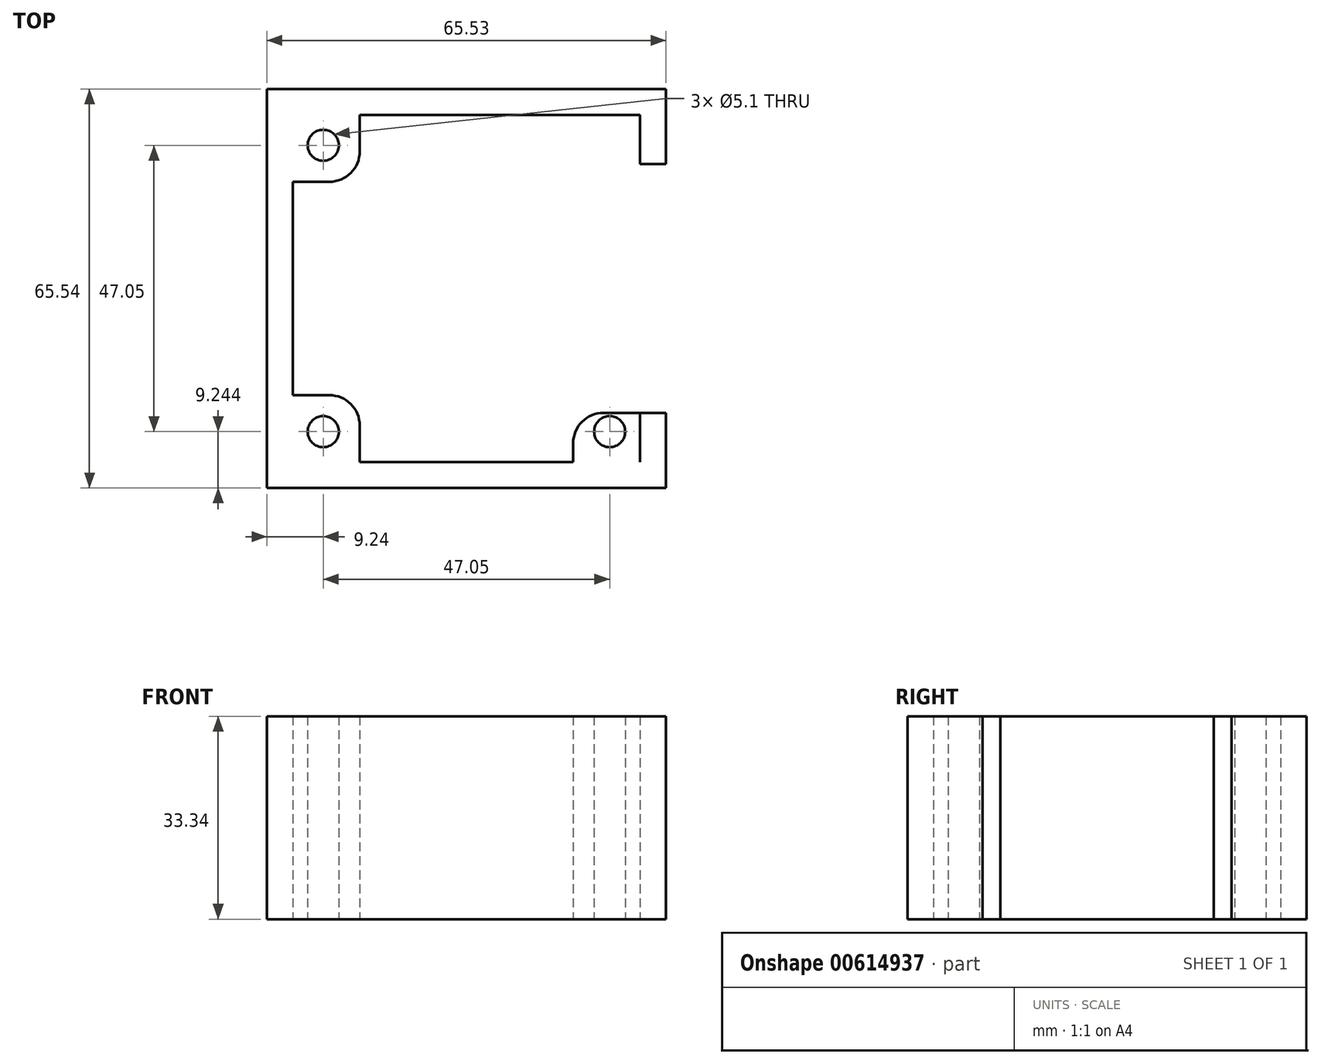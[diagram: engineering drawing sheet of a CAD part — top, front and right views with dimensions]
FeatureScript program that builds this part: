
annotation { "Feature Type Name" : "Feature", "Feature Type Description" : "" }
export const myFeature = defineFeature(function(context is Context, id is Id, definition is map)
    precondition{}
    {
        {
            var Q0;
            Q0=qCreatedBy(makeId("Top.planeOp"),FACE);
            var sketch = newSketch(context, id + "F0", { "sketchPlane" : qUnion([Q0])});
            skLineSegment(sketch, "E0", {"start": v(57.55, -8.14) * mm, "end": v(-2.45, -8.14) * mm});
            skLineSegment(sketch, "E1.bottom", {"start": v(26.08, 20.38) * mm, "end": v(-30.97, 20.38) * mm});
            skLineSegment(sketch, "E1.top", {"start": v(26.08, -36.67) * mm, "end": v(-30.97, -36.67) * mm});
            skLineSegment(sketch, "E1.left", {"start": v(26.08, 20.38) * mm, "end": v(26.08, -36.67) * mm});
            skLineSegment(sketch, "E1.right", {"start": v(-30.97, 20.38) * mm, "end": v(-30.97, -36.67) * mm});
            skPoint(sketch, "E1.middle", {"position": v(-2.45, -8.14) * mm});
            skLineSegment(sketch, "E2.bottom", {"start": v(30.32, 24.63) * mm, "end": v(-35.21, 24.63) * mm});
            skLineSegment(sketch, "E2.top", {"start": v(30.32, -40.9) * mm, "end": v(-35.21, -40.9) * mm});
            skLineSegment(sketch, "E2.left", {"start": v(30.32, 24.63) * mm, "end": v(30.32, -40.9) * mm});
            skLineSegment(sketch, "E2.right", {"start": v(-35.21, 24.63) * mm, "end": v(-35.21, -40.9) * mm});
            skLineSegment(sketch, "E3", {"start": v(26.08, 20.38) * mm, "end": v(30.32, 24.63) * mm});
            skLineSegment(sketch, "E4", {"start": v(26.08, 20.38) * mm, "end": v(26.08, 12.3) * mm});
            skLineSegment(sketch, "E5", {"start": v(26.08, 12.3) * mm, "end": v(30.32, 12.3) * mm});
            skLineSegment(sketch, "E6", {"start": v(30.32, 12.3) * mm, "end": v(30.32, 24.63) * mm});
            skLineSegment(sketch, "E7.MirrorCS", {"start": v(26.08, -28.57) * mm, "end": v(30.33, -28.57) * mm});
            skLineSegment(sketch, "E8.MirrorCS", {"start": v(30.33, -28.57) * mm, "end": v(30.33, -40.9) * mm});
            skLineSegment(sketch, "E9", {"start": v(26.08, -28.57) * mm, "end": v(26.08, -36.67) * mm});
            skLineSegment(sketch, "E10", {"start": v(-30.97, 20.38) * mm, "end": v(-25.97, 15.38) * mm});
            skCircle(sketch, "E11", {"center": v(-25.97, 15.38) * mm, "radius": 2.55 * mm});
            skLineSegment(sketch, "E12.bottom", {"start": v(-30.97, 20.38) * mm, "end": v(-19.97, 20.38) * mm});
            skLineSegment(sketch, "E12.top", {"start": v(-30.97, 9.38) * mm, "end": v(-24.97, 9.38) * mm});
            skLineSegment(sketch, "E12.left", {"start": v(-30.97, 20.38) * mm, "end": v(-30.97, 9.38) * mm});
            skLineSegment(sketch, "E12.right", {"start": v(-19.97, 20.38) * mm, "end": v(-19.97, 14.38) * mm});
            skPoint(sketch, "E13.visualSharp", {"position": v(-19.97, 9.38) * mm});
            skArc(sketch, "E13.filletArc", {"start": v(-24.97, 9.38) * mm, "mid": v(-21.43, 10.85) * mm, "end": v(-19.97, 14.38) * mm});
            skLineSegment(sketch, "E14", {"start": v(26.08, 20.38) * mm, "end": v(21.08, 15.38) * mm});
            skCircle(sketch, "E15", {"center": v(21.08, 15.38) * mm, "radius": 2.55 * mm});
            skLineSegment(sketch, "E16", {"start": v(26.08, 12.3) * mm, "end": v(20.08, 12.3) * mm});
            skLineSegment(sketch, "E17", {"start": v(15.08, 17.3) * mm, "end": v(15.08, 20.38) * mm});
            skPoint(sketch, "E18.visualSharp", {"position": v(15.08, 12.3) * mm});
            skArc(sketch, "E18.filletArc", {"start": v(15.08, 17.3) * mm, "mid": v(16.54, 13.76) * mm, "end": v(20.08, 12.3) * mm});
            skLineSegment(sketch, "E19", {"start": v(-30.97, -36.67) * mm, "end": v(-25.97, -31.67) * mm});
            skLineSegment(sketch, "E20", {"start": v(-19.97, -36.67) * mm, "end": v(-19.97, -30.67) * mm});
            skLineSegment(sketch, "E21", {"start": v(-24.97, -25.67) * mm, "end": v(-30.97, -25.67) * mm});
            skPoint(sketch, "E22.visualSharp", {"position": v(-19.97, -25.67) * mm});
            skArc(sketch, "E22.filletArc", {"start": v(-19.97, -30.67) * mm, "mid": v(-21.43, -27.13) * mm, "end": v(-24.97, -25.67) * mm});
            skCircle(sketch, "E23", {"center": v(-25.97, -31.67) * mm, "radius": 2.55 * mm});
            skLineSegment(sketch, "E24", {"start": v(26.08, -36.67) * mm, "end": v(21.08, -31.67) * mm});
            skLineSegment(sketch, "E25", {"start": v(15.08, -33.57) * mm, "end": v(15.08, -36.67) * mm});
            skCircle(sketch, "E26", {"center": v(21.08, -31.67) * mm, "radius": 2.55 * mm});
            skLineSegment(sketch, "E27", {"start": v(26.08, -28.57) * mm, "end": v(20.08, -28.57) * mm});
            skLineSegment(sketch, "E28", {"start": v(15.08, -33.57) * mm, "end": v(15.08, -33.57) * mm});
            skPoint(sketch, "E29.visualSharp", {"position": v(15.08, -28.57) * mm});
            skArc(sketch, "E29.filletArc", {"start": v(20.08, -28.57) * mm, "mid": v(16.55, -30.04) * mm, "end": v(15.08, -33.57) * mm});
            skSolve(sketch);
        }
        {
            var Q0;
            Q0=makeQuery(id+"F0.imprint","IMPRINT",FACE,{"disambiguationData":[TD([[makeQuery(id+"F0.imprint","IMPRINT",EDGE,{"derivedFrom":sQuery(id+"F0.wireOp",EDGE,"E2.bottom")}),1.0]])]});
            var Q1;
            Q1=makeQuery(id+"F0.imprint","IMPRINT",FACE,{"disambiguationData":[TD([[makeQuery(id+"F0.imprint","IMPRINT",EDGE,{"derivedFrom":sQuery(id+"F0.wireOp",EDGE,"E11")}),-1.0]])]});
            var Q2;
            {var subQ0=sQuery(id+"F0.wireOp",EDGE,"E4");Q2=makeQuery(id+"F0.imprint","IMPRINT",FACE,{"disambiguationData":[TD([[makeQuery(id+"F0.imprint","IMPRINT",EDGE,{"derivedFrom":subQ0}),-1.0]])]});}
            var Q3;
            {var subQ0=sQuery(id+"F0.wireOp",EDGE,"E25");Q3=makeQuery(id+"F0.imprint","IMPRINT",FACE,{"disambiguationData":[TD([[makeQuery(id+"F0.imprint","IMPRINT",EDGE,{"derivedFrom":subQ0}),1.0]])]});}
            var Q4;
            {var subQ1=sQuery(id+"F0.wireOp",EDGE,"E20");Q4=makeQuery(id+"F0.imprint","IMPRINT",FACE,{"disambiguationData":[TD([[makeQuery(id+"F0.imprint","IMPRINT",EDGE,{"derivedFrom":subQ1}),1.0]])]});}
            var Q5;
            Q5=makeQuery(id+"F0.imprint","IMPRINT",FACE,{"disambiguationData":[TD([[makeQuery(id+"F0.imprint","IMPRINT",EDGE,{"derivedFrom":sQuery(id+"F0.wireOp",EDGE,"E3")}),-1.0]])]});
            extrude(context, id + "F1", {"entities" : qUnion([Q0, Q1, Q2, Q3, Q4, Q5]), "depth" : 33.34 * mm, "offsetDistance" : 25 * mm});
        }
    });
